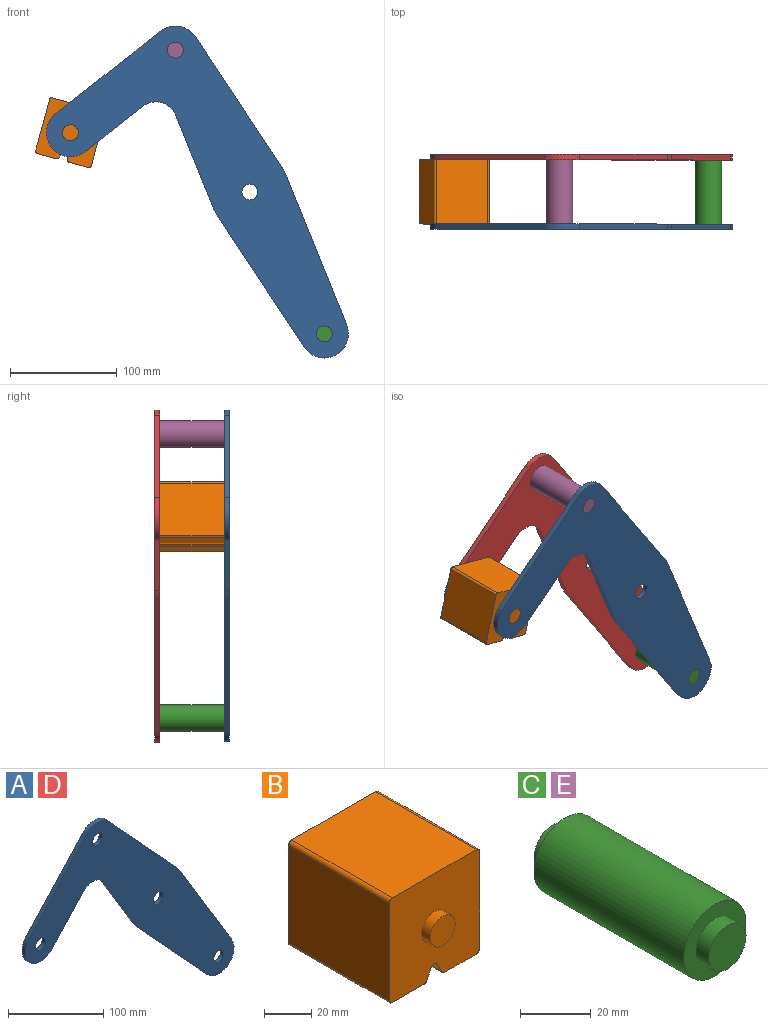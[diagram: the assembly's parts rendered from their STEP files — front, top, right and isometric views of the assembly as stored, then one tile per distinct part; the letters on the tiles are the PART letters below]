
ASSEMBLY  parts=5 mates=3
PART A: 18 faces, bbox 309.5x5x285.1 mm
  f0: cylinder r=22.5mm len=39.07mm, axis (0,1,0), area 353.4mm2, adj f1,f13,f16,f17
  f1: plane 50.28x46.21mm, normal (0.74,0,-0.68), area 341.4mm2, adj f0,f2,f16,f17
  f2: cylinder r=20mm len=31.85mm, axis (0,1,0), area 185.5mm2, adj f1,f3,f16,f17
  f3: plane 79.23x47.81mm, normal (-0.86,0,-0.52), area 462.7mm2, adj f2,f4,f16,f17
  f4: cylinder r=37.5mm len=6mm, axis (0,1,0), area 37.6mm2, adj f3,f5,f16,f17
  f5: plane 109.88x101mm, normal (-0.74,0,-0.68), area 746.2mm2, adj f4,f6,f16,f17
  f6: cylinder r=22.5mm len=39.07mm, axis (0,1,0), area 330.9mm2, adj f5,f7,f16,f17
  f7: plane 127.78x77.11mm, normal (0.86,0,0.52), area 746.2mm2, adj f6,f8,f16,f17
  f8: cylinder r=37.5mm len=6mm, axis (0,1,0), area 37.6mm2, adj f7,f9,f16,f17
  f9: plane 109.88x101mm, normal (0.74,0,0.68), area 746.2mm2, adj f8,f10,f16,f17
  f10: cylinder r=22.5mm len=33.13mm, axis (0,1,0), area 186.2mm2, adj f9,f13,f16,f17
  f11: cylinder r=7.5mm len=15mm, axis (0,1,0), area 235.6mm2, adj f16,f17
  f12: cylinder r=7.5mm len=15mm, axis (0,1,0), area 235.6mm2, adj f16,f17
  f13: plane 92.03x84.59mm, normal (-0.74,0,0.68), area 625mm2, adj f0,f10,f16,f17
  f14: cylinder r=7.5mm len=15mm, axis (0,1,0), area 235.6mm2, adj f16,f17
  f15: cylinder r=7.5mm len=15mm, axis (0,1,0), area 235.6mm2, adj f16,f17
  f16: plane 309.5x285.07mm, normal (0,-1,0), area 24555.4mm2, adj f0,f1,f2,f3,f4,f5,f6,f7
  f17: plane 309.5x285.07mm, normal (0,1,0), area 24555.4mm2, adj f0,f1,f2,f3,f4,f5,f6,f7
PART B: 20 faces, bbox 54x70x54 mm
  f0: plane 60x50.01mm, normal (-1,0,0), area 3000.4mm2, adj f7,f10,f13,f19
  f1: plane 60x50.01mm, normal (0,0,1), area 3000.4mm2, adj f7,f10,f13,f14
  f2: plane 60x50.01mm, normal (1,0,0), area 3000.4mm2, adj f7,f10,f14,f15
  f3: plane 60x18.77mm, normal (0,0,-1), area 1126mm2, adj f7,f10,f15,f16
  f4: plane 60x5.32mm, normal (-0.89,0,-0.45), area 356.7mm2, adj f7,f10,f16,f17
  f5: plane 60x5.32mm, normal (0.89,0,-0.45), area 356.7mm2, adj f7,f10,f17,f18
  f6: plane 60x18.77mm, normal (0,0,-1), area 1126mm2, adj f7,f10,f18,f19
  f7: plane 54.01x54.01mm, normal (0,-1,0), area 2689.6mm2, adj f0,f1,f2,f3,f4,f5,f6,f9
  f8: plane 15x15mm, normal (0,-1,0), area 176.7mm2, adj f9
  f9: cylinder r=7.5mm len=15mm, axis (0,1,0), area 235.6mm2, adj f7,f8
  f10: plane 54.01x54.01mm, normal (0,1,0), area 2689.6mm2, adj f0,f1,f2,f3,f4,f5,f6,f12
  f11: plane 15x15mm, normal (0,1,0), area 176.7mm2, adj f12
  f12: cylinder r=7.5mm len=15mm, axis (0,-1,0), area 235.6mm2, adj f10,f11
  f13: cylinder r=2mm len=60mm, axis (0,-1,0), area 188.5mm2, adj f0,f1,f7,f10
  f14: cylinder r=2mm len=60mm, axis (0,1,0), area 188.5mm2, adj f1,f2,f7,f10
  f15: cylinder r=2mm len=60mm, axis (0,-1,0), area 188.5mm2, adj f2,f3,f7,f10
  f16: cylinder r=2mm len=60mm, axis (0,-1,0), area 132.9mm2, adj f3,f4,f7,f10
  f17: cylinder r=2mm len=60mm, axis (0,-1,0), area 265.7mm2, adj f4,f5,f7,f10
  f18: cylinder r=2mm len=60mm, axis (0,1,0), area 132.9mm2, adj f5,f6,f7,f10
  f19: cylinder r=2mm len=60mm, axis (0,1,0), area 188.5mm2, adj f0,f6,f7,f10
PART C: 7 faces, bbox 25x70x25 mm
  f0: cylinder r=12.5mm len=60mm, axis (0,-1,0), area 4712.4mm2, adj f2,f5
  f1: cylinder r=7.5mm len=15mm, axis (0,1,0), area 235.6mm2, adj f2,f3
  f2: plane 25x25mm, normal (0,-1,0), area 314.2mm2, adj f0,f1
  f3: plane 15x15mm, normal (0,-1,0), area 176.7mm2, adj f1
  f4: cylinder r=7.5mm len=15mm, axis (0,-1,0), area 235.6mm2, adj f5,f6
  f5: plane 25x25mm, normal (0,1,0), area 314.2mm2, adj f0,f4
  f6: plane 15x15mm, normal (0,1,0), area 176.7mm2, adj f4
PART D: same geometry as A
PART E: same geometry as C
PLACE A rot(axis=(0,1,0),9.2deg) t=(0,-30,0)mm fixed
PLACE B rot(axis=(0,1,0),15.1deg) t=(-6.7,-30,-17.22)mm
PLACE C rot(axis=(0,1,0),9.2deg) t=(139.44,-30,-265.63)mm
PLACE D rot(axis=(0,1,0),9.2deg) t=(0,35,0)mm
PLACE E rot(axis=(0,1,0),9.2deg) t=(0,-30,0)mm
MATE fastened D.f10 <-> E.f0  axis (0,-1,0) through (-69.72,30,132.81)mm
MATE revolute B.f9 <-> A.f0  axis (0,1,0) through (-167.87,-30,55.41)mm
MATE fastened C.f0 <-> A.f6  axis (0,1,0) through (69.72,-30,-132.81)mm
